# Revit family: 240716_Jungle Box
name_source: partatom
category: Generic Models
units: mm (PartAtom-declared; Revit-internal decimal feet)

## family parameters
Always vertical = Yes
Can host rebar = No
Cut with Voids When Loaded = No
Maintain Annotation Orientation = No
Part Type = Normal
Room Calculation Point = No
Round Connector Dimension = Use Diameter
Shared = No
Work Plane-Based = Yes

## types (1)
- 240716_Jungle Box
    Default Elevation = 0 mm  [stored 0 ft]
    Dry Weight = 17.00 kg
    Irrigation = Dripline clickable in clamp on top of crate
    Length = 600 mm
    Saturated Weight = 31.00 kg
    Waterbuffering Capacity = 68.4 L/m²
    Weight per m2 Saturated = 130.00 kg/m²
    Width = 400 mm  [stored 1.31234 ft]
    material_01 = 3D Printed Frame

note: [stored X ft] marks values corroborated as IEEE doubles in the binary element streams (Revit-internal decimal feet)

## geometry (parser evidence)
native form markers: Sweep x10
no freeform markers — native parametric forms only
